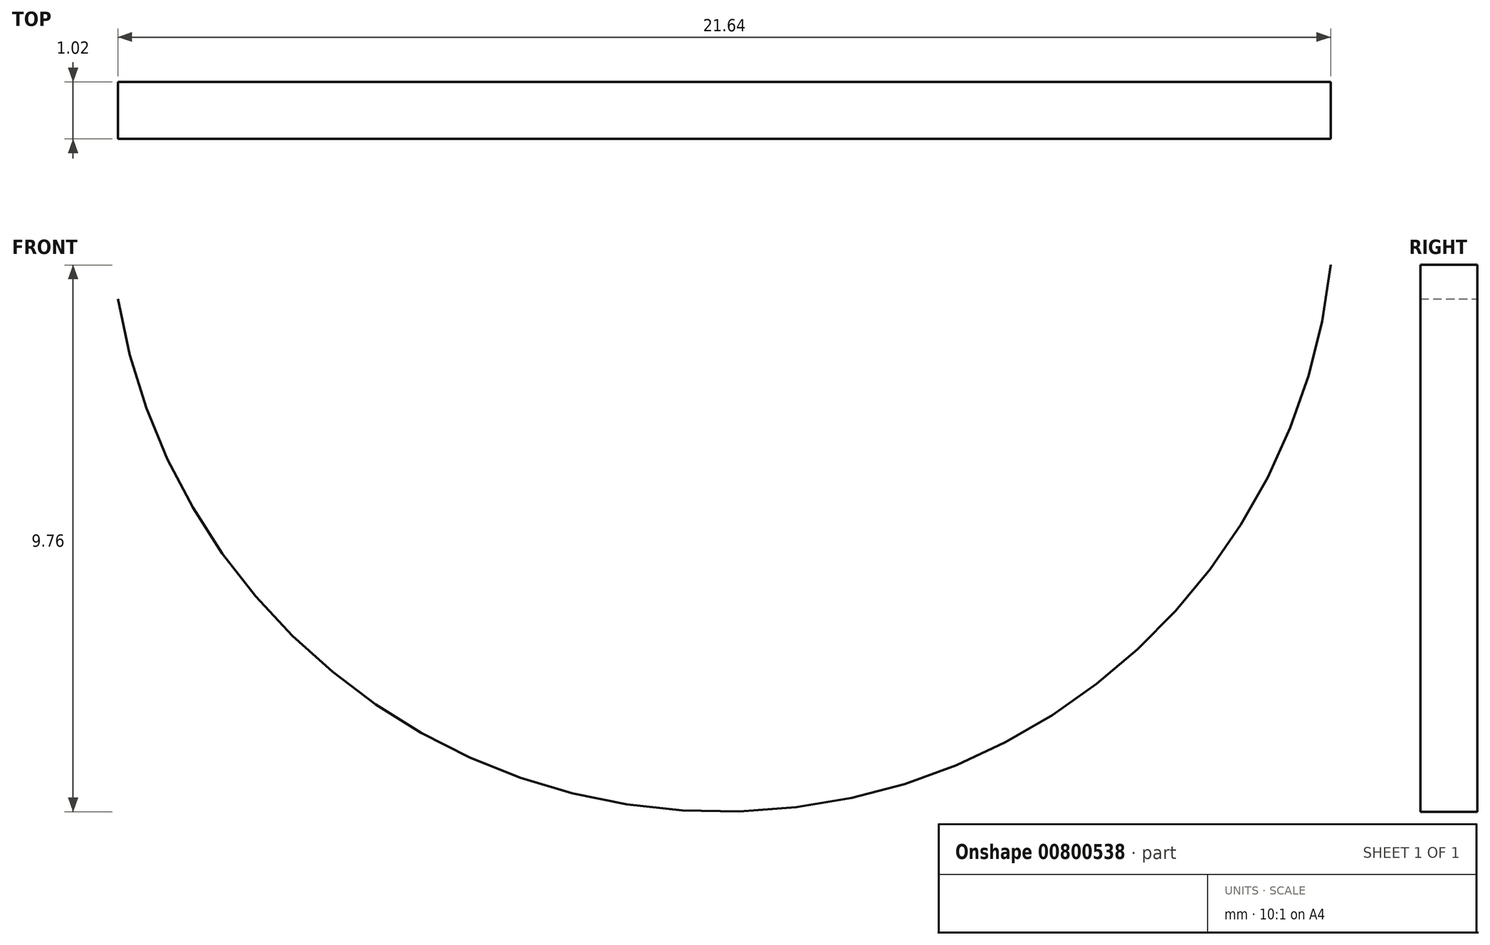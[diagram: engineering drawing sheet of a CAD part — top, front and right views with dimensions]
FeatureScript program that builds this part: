
annotation { "Feature Type Name" : "Feature", "Feature Type Description" : "" }
export const myFeature = defineFeature(function(context is Context, id is Id, definition is map)
    precondition{}
    {
        {
            var Q0;
            Q0=qCreatedBy(makeId("Front.planeOp"),FACE);
            var sketch = newSketch(context, id + "F0", { "sketchPlane" : qUnion([Q0])});
            skArc(sketch, "E0", {"start": v(-57.99, 26.44) * mm, "mid": v(-46.9, 17.3) * mm, "end": v(-36.35, 27.05) * mm});
            skSolve(sketch);
        }
        {
            var Q0;
            Q0=sQuery(id+"F0.wireOp",EDGE,"E0");
            extrude(context, id + "F1", {"bodyType" : ToolBodyType.SURFACE, "surfaceEntities" : qUnion([Q0]), "oppositeDirection" : true, "depth" : 1.02 * mm, "offsetDistance" : 25.4 * mm});
        }
    });
